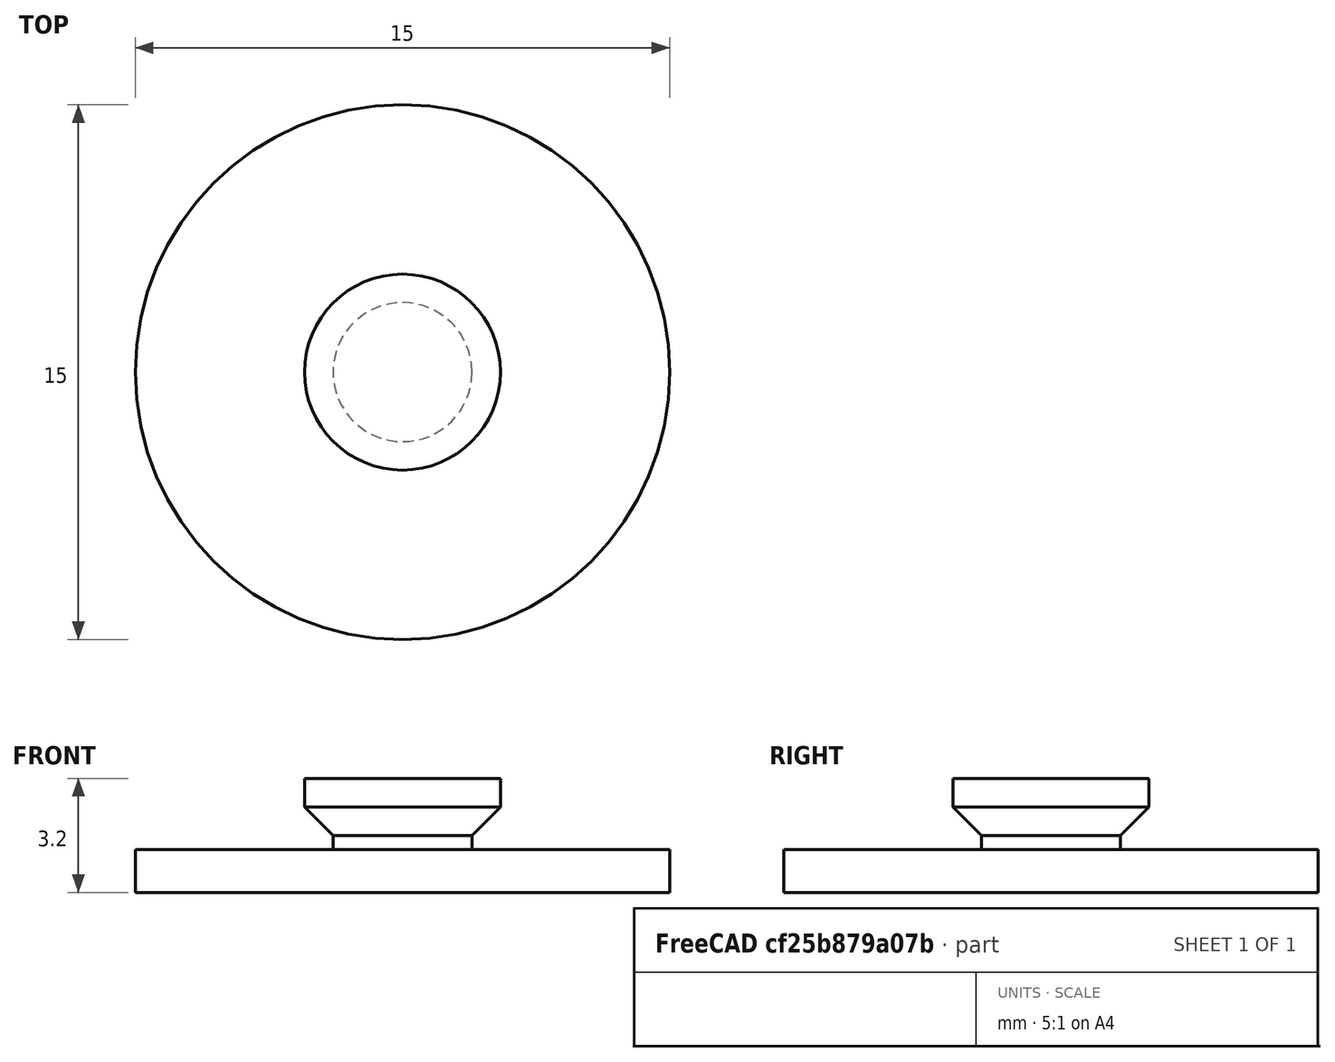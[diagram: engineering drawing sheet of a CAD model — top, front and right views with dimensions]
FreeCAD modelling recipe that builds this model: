
FCSTD DOCUMENT  (FreeCAD 0.19R)
Label: hook_sign_small
License: All rights reserved
LicenseURL: http://en.wikipedia.org/wiki/All_rights_reserved
objects: Sketcher::SketchObject×1, PartDesign::Revolution×1, PartDesign::Body×1
note: 4 computed .brp shape members not serialized (recipe doc carries the construction recipe); baked Part::Feature solids carry a one-line shape summary decoded from their .brp

FEATURE [Sketcher::SketchObject] Sketch
  FullyConstrained = true
  MapMode = 5
  Placement = pos=(0,0,0) rot=(1,0,0;1.5708rad)
  Support = -> [XZ_Plane]
  sketch-geometry (8):
    g0: LineSegment StartX=0 StartY=0 StartZ=0 EndX=-7.5 EndY=0 EndZ=0
    g1: LineSegment StartX=-7.5 StartY=0 StartZ=0 EndX=-7.5 EndY=1.2 EndZ=0
    g2: LineSegment StartX=-7.5 StartY=1.2 StartZ=0 EndX=-1.95 EndY=1.2 EndZ=0
    g3: LineSegment StartX=-1.95 StartY=1.2 StartZ=0 EndX=-1.95 EndY=1.6 EndZ=0
    g4: LineSegment StartX=-1.95 StartY=1.6 StartZ=0 EndX=-2.75 EndY=2.4 EndZ=0
    g5: LineSegment StartX=-2.75 StartY=2.4 StartZ=0 EndX=-2.75 EndY=3.2 EndZ=0
    g6: LineSegment StartX=-2.75 StartY=3.2 StartZ=0 EndX=0 EndY=3.2 EndZ=0
    g7: LineSegment StartX=0 StartY=3.2 StartZ=0 EndX=0 EndY=0 EndZ=0
  constraints (23):
    c: Coincident(g-1,g0)
    c: Horizontal(g0)
    c: Coincident(g0,g1)
    c: Vertical(g1)
    c: Coincident(g1,g2)
    c: Horizontal(g2)
    c: Coincident(g2,g3)
    c: Vertical(g3)
    c: Coincident(g3,g4)
    c: Coincident(g4,g5)
    c: Vertical(g5)
    c: Coincident(g5,g6)
    c: Horizontal(g6)
    c: Coincident(g6,g7)
    c: Coincident(g7,g0)
    c: Vertical(g7)
    c: DistanceX(g0,g0) = 7.5
    c: DistanceY(g1,g1) = 1.2
    c: DistanceX(g6,g6) = 2.75
    c: DistanceX(g4,g4) = 0.8
    c: DistanceY(g5,g5) = 0.8
    c: DistanceY(g3,g3) = 0.4
    c: DistanceY(g2,g4) = 1.2
FEATURE [PartDesign::Revolution] Revolution
  Angle = 360
  Axis = (0,2e-16,1)
  Base = (0,0,0)
  Placement = pos=(0,0,0) rot=(1,0,0;1.5708rad)
  Profile = -> Sketch
  ReferenceAxis = -> Sketch [V_Axis]
  Refine = true
FEATURE [PartDesign::Body] Body
  Group = -> [Sketch,Revolution]
  Origin = -> Origin
  Tip = -> Revolution
